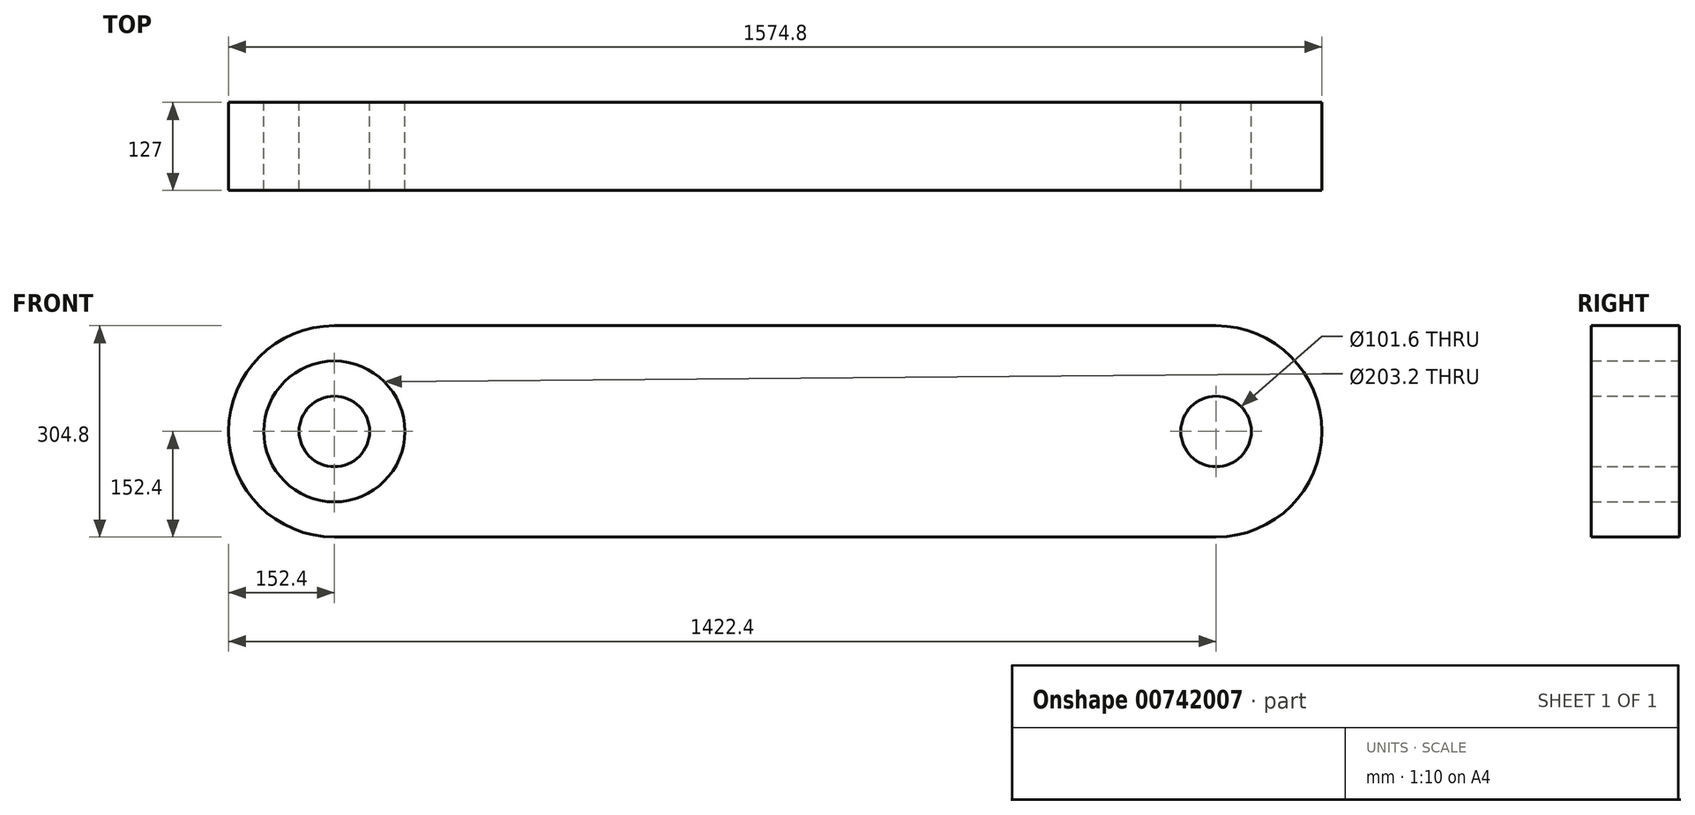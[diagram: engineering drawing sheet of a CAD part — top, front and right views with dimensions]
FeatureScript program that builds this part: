
annotation { "Feature Type Name" : "Feature", "Feature Type Description" : "" }
export const myFeature = defineFeature(function(context is Context, id is Id, definition is map)
    precondition{}
    {
        {
            var Q0;
            Q0=qCreatedBy(makeId("Front.planeOp"),FACE);
            var sketch = newSketch(context, id + "F0", { "sketchPlane" : qUnion([Q0])});
            skCircle(sketch, "E0", {"center": v(-635, 0) * mm, "radius": 50.8 * mm});
            skCircle(sketch, "E1", {"center": v(-635, 0) * mm, "radius": 101.6 * mm});
            skCircle(sketch, "E2", {"center": v(-635, 0) * mm, "radius": 152.4 * mm});
            skLineSegment(sketch, "E3", {"start": v(-635, 152.4) * mm, "end": v(0, 152.4) * mm});
            skLineSegment(sketch, "E4.MirrorCS", {"start": v(-635, -152.4) * mm, "end": v(0, -152.4) * mm});
            skCircle(sketch, "E5.MirrorC", {"center": v(635, 0) * mm, "radius": 152.4 * mm});
            skCircle(sketch, "E6.MirrorC", {"center": v(635, 0) * mm, "radius": 101.6 * mm});
            skLineSegment(sketch, "E7.MirrorCS", {"start": v(635, 152.4) * mm, "end": v(0, 152.4) * mm});
            skCircle(sketch, "E8.MirrorC", {"center": v(635, 0) * mm, "radius": 50.8 * mm});
            skLineSegment(sketch, "E9.MirrorCS", {"start": v(635, -152.4) * mm, "end": v(0, -152.4) * mm});
            skSolve(sketch);
        }
        {
            var Q0;
            Q0 = qSketchRegion(id + "F0", true);
            var Q1;
            Q1=makeQuery(id+"F0.imprint","IMPRINT",FACE,{"disambiguationData":[TD([[makeQuery(id+"F0.imprint","IMPRINT",EDGE,{"derivedFrom":sQuery(id+"F0.wireOp",EDGE,"E8.MirrorC")}),-1.0]])]});
            var Q2;
            Q2=makeQuery(id+"F0.imprint","IMPRINT",FACE,{"disambiguationData":[TD([[makeQuery(id+"F0.imprint","IMPRINT",EDGE,{"derivedFrom":sQuery(id+"F0.wireOp",EDGE,"E0")}),1.0]])]});
            extrude(context, id + "F1", {"entities" : qUnion([Q0, Q1, Q2]), "endBound" : BoundingType.SYMMETRIC, "depth" : 127 * mm, "offsetDistance" : 25.4 * mm});
        }
    });
